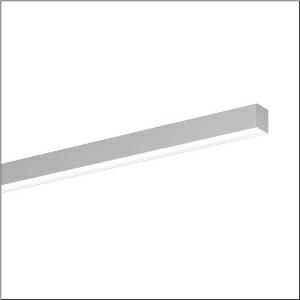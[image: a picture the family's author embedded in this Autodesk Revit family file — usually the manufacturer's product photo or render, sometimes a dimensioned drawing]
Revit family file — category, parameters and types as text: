
# Revit family: silica_21_51mx20dc45sb
name_source: partatom
category: Lighting Fixtures
units: mm (PartAtom-declared; Revit-internal decimal feet)

## family parameters
Cut with Voids When Loaded = No
Host = Face
Light Source = No
Part Type = Normal
Room Calculation Point = No
Round Connector Dimension = Use Diameter
Shared = No

## types (1)
- --- (1 x LED, 6000 lm, 40.1 W, 4000K)
    Apparent Load = 40 VA
    CIE Flux Codes = 48 79 96 100 100
    Color Rendering = 80
    Color Temperature = 4000K
    Default Elevation = 1800 mm
    Description = Silica 21, office luminaire, primary optical cover: cover, of PMMA, opal, light emission: direct distribution, primary light characteristic: symmetric, installation type: surface-mounted, LED, rated luminous flux: 6.000lm, luminous efficacy: 150lm/W, light colour: 840, colour temperature: 4000K, control gear: DALI 2, with terminal, 3+2-pole, max. 2.5mm², mains connection: 220..240V, AC, 50/60Hz, rated input power: 40.1W, luminaire housing, of aluminium, metallic grey (RAL 9006), length: 3.004mm, width: 53mm, height: 53mm, protection rating (complete): IP20, insulation class (complete): insulation class I (protective earthing), certification: CE, permissible operating ambient temperature: 0..+35°C, standard: EN 50419, packaging unit: 1 piece
    Height = 53 mm
    Lamp = 1 x LED
    Lamp Light Flux = 6000 lm
    Lamp Power = 40.1 W
    Lamp count = 1
    Length = 3004 mm
    Luminous efficacy = 150 lm/W
    Manufacturer = Siteco
    ModVariant = No
    Model = 51MX20DC45SB
    Mounting Place = Ceiling
    Mounting Type = Surface mounted
    Number of Poles = 1
    OnlyDefault = Yes
    Power Factor = 1
    Product Name = Silica 21
    Product group = office luminaire | ceiling mounted
    ProductGroupID = 301
    Protection Class = Protection class I
    Protection Degree = IP 20
    RLX_Detail_Level = 1
    RLX_Emergency_Light_Flux = 0 lm
    RLX_Emergency_Type = 0
    RLX_Emergency_Type_DB = No
    RlxData = <blob elided: 26421 chars, md5=646869d9>
    Socket = socket
    Standby Power = 0 W
    System Light Flux = 6000 lm
    System Power = 40 W
    Type Comments = factory setting: luminous flux: 100 % | dim-lin: 254 | 218 mA
    Type Image = l_1335933.jpg
    URL = http://relux.com
    VarID = @adj_117927
    Voltage = 0 V
    Weight = 0.00 kg
    Width = 53 mm

## geometry (parser evidence)
native form markers: Blend x4, Sweep x11
no freeform markers — native parametric forms only
